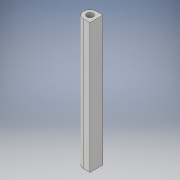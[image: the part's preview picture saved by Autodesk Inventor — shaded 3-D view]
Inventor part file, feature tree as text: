
AUTODESK INVENTOR PART (.ipt)
format: ipt  version: 2017 (Build 210142000, 142)  size: 97,792 bytes
history: native  units: in
note: dims shown in document units (in); Inventor stores cm internally (conversion verified against a paired STEP export)
features: extrude x1
ambient origin geometry x8: Origin, YZ Plane, XZ Plane, XY Plane, X Axis, Y Axis, Z Axis, Center Point
bodies: Solid1 (feature_tree)
feature tree (1):
  extrude  "Extrusion1"  Depth=0.125in
